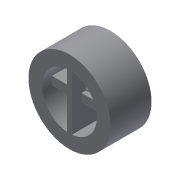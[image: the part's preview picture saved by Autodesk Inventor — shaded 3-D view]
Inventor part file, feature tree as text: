
AUTODESK INVENTOR PART (.ipt)
format: ipt  version: 2014 SP1 (Build 180222100, 222)  size: 152,576 bytes
history: native  units: in
note: dims shown in document units (in); Inventor stores cm internally (conversion verified against a paired STEP export)
features: sketch x5, extrude x4, revolve x1
ambient origin geometry x8: Origin, YZ Plane, XZ Plane, XY Plane, X Axis, Y Axis, Z Axis, Center Point
bodies: Solid1 (feature_tree)
feature tree (10):
  revolve  "Revolution1"  [1 undecoded]
  extrude  "Extrusion1"  Depth=0.1in
  extrude  "Extrusion2"  Depth=0.1in
  extrude  "Extrusion3"  Depth=0.025in
  extrude  "Extrusion4"  Depth=0.13in
  sketch  "Sketch1"  dims[d0=0.3in d1=0.1in]
  sketch  "Sketch2"  dims[d2=0.2in d3=0.1in]
  sketch  "Sketch3"  dims[d4=0.05in d5=0.1in]
  sketch  "Sketch4"  dims[d6=90.0deg d7=0.025in]
  sketch  "Sketch5"  dims[d8=0.07in d9=0.025in d10=1.0in d11=0.0in d12=0.025in d13=0.025in d14=0.025in d15=0.025in d16=0.025in d17=0.025in d18=1.0in d19=0.0in d20=0.2in d21=0.0in d22=0.13in d23=0.0in]
note: 1 required parameter value undecoded (feature->parameter linkage not recoverable at this tier; creation-order binding heuristic only, values carry confidence <= 0.55)
